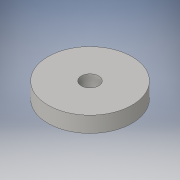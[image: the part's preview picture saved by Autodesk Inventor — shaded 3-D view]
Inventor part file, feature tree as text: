
AUTODESK INVENTOR PART (.ipt)
format: ipt  version: 2016 (Build 200138000, 138)  size: 91,648 bytes
history: native  units: in
note: dims shown in document units (in); Inventor stores cm internally (conversion verified against a paired STEP export)
features: extrude x1, sketch x1
ambient origin geometry x8: Origin, YZ Plane, XZ Plane, XY Plane, X Axis, Y Axis, Z Axis, Center Point
bodies: Solid1 (feature_tree)
feature tree (2):
  extrude  "Extrusion1"  Depth=0.75in
  sketch  "Sketch1"  dims[d0=0.8268in d1=4.0in d2=0.75in d3=0.0in]
